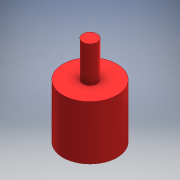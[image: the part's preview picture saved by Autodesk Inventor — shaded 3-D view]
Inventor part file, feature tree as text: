
AUTODESK INVENTOR PART (.ipt)
format: ipt  version: 2020.2 (Build 242310000, 310)  size: 103,936 bytes
history: native  units: mm
features: other x2, sketch x2, extrude x2, hole x1
ambient origin geometry x8: Origin, YZ Plane, XZ Plane, XY Plane, X Axis, Y Axis, Z Axis, Center Point
bodies: Body1 (feature_tree)
feature tree (7):
  other  "ソリッド1"
  sketch  "スケッチ1"
  extrude  "押し出し1"  Depth=15.0mm
  extrude  "押し出し2"  Depth=4.0mm
  hole  "穴1"  [1 undecoded]
  sketch  "スケッチ2"
  other  "断面エッジを投影1"
note: 1 required parameter value undecoded (feature->parameter linkage not recoverable at this tier; creation-order binding heuristic only, values carry confidence <= 0.55)
